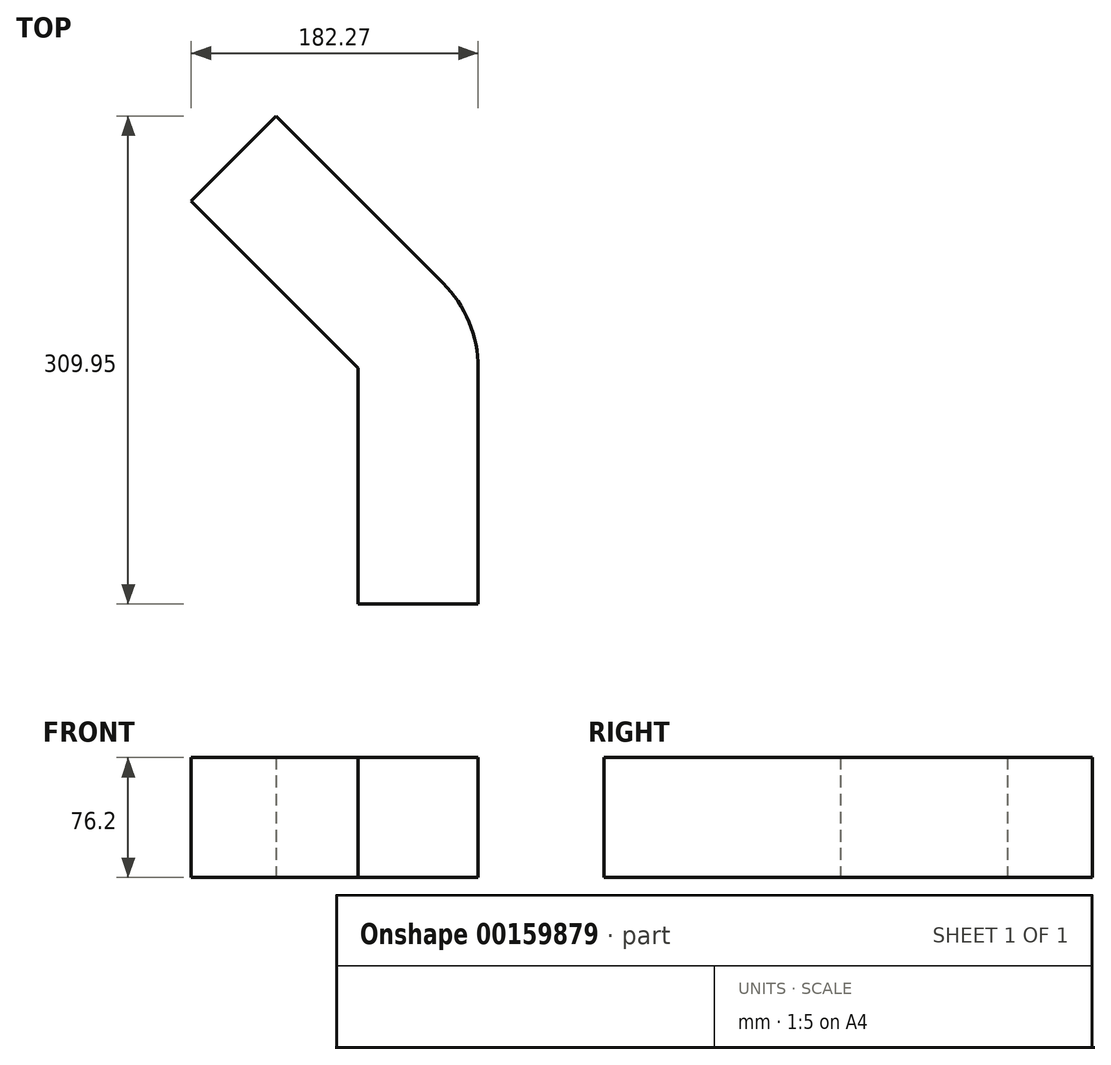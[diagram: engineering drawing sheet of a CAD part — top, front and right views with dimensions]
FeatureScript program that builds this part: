
annotation { "Feature Type Name" : "Feature", "Feature Type Description" : "" }
export const myFeature = defineFeature(function(context is Context, id is Id, definition is map)
    precondition{}
    {
        {
            var Q0;
            Q0=qCreatedBy(makeId("Top.planeOp"),FACE);
            var sketch = newSketch(context, id + "F0", { "sketchPlane" : qUnion([Q0])});
            skArc(sketch, "E0", {"start": v(76.2, 0) * mm, "mid": v(70.4, 29.16) * mm, "end": v(53.88, 53.88) * mm});
            skLineSegment(sketch, "E1", {"start": v(0, 0) * mm, "end": v(-106.07, 106.07) * mm});
            skLineSegment(sketch, "E2", {"start": v(-106.07, 106.07) * mm, "end": v(-52.18, 159.95) * mm});
            skLineSegment(sketch, "E3", {"start": v(-52.18, 159.95) * mm, "end": v(53.88, 53.88) * mm});
            skLineSegment(sketch, "E4", {"start": v(0, 0) * mm, "end": v(0, -150) * mm});
            skLineSegment(sketch, "E5", {"start": v(0, -150) * mm, "end": v(76.2, -150) * mm});
            skLineSegment(sketch, "E6", {"start": v(76.2, -150) * mm, "end": v(76.2, 0) * mm});
            skSolve(sketch);
        }
        {
            var Q0;
            Q0 = qSketchRegion(id + "F0", true);
            extrude(context, id + "F1", {"entities" : qUnion([Q0]), "depth" : 76.2 * mm});
        }
    });
